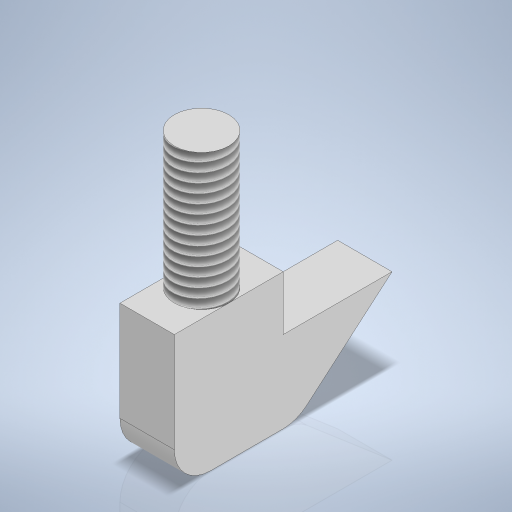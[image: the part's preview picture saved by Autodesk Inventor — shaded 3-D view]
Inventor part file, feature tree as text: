
AUTODESK INVENTOR PART (.ipt)
format: ipt  version: 2024 (Build 280153000, 153)  size: 270,848 bytes
history: native  units: mm
features: extrude x2, sketch x2, thread x1
ambient origin geometry x8: Origin, YZ Plane, XZ Plane, XY Plane, X Axis, Y Axis, Z Axis, Center Point
bodies: Volumenkörper1 (feature_tree)
feature tree (5):
  extrude  "Extrusion1"  Depth=6.0mm
  extrude  "Extrusion2"  Depth=6.0mm
  thread  "Gewinde1"  [1 undecoded]
  sketch  "Skizze1"  dims[d3=3.0mm d4=6.0mm]
  sketch  "Skizze2"  dims[d8=2.0mm d9=6.0mm d10=7.5mm d11=3.0mm d12=0.0mm d13=3.0mm d14=3.0mm d15=7.5mm d16=0.0mm d17=11.0mm d18=0.0mm]
note: 1 required parameter value undecoded (feature->parameter linkage not recoverable at this tier; creation-order binding heuristic only, values carry confidence <= 0.55)
